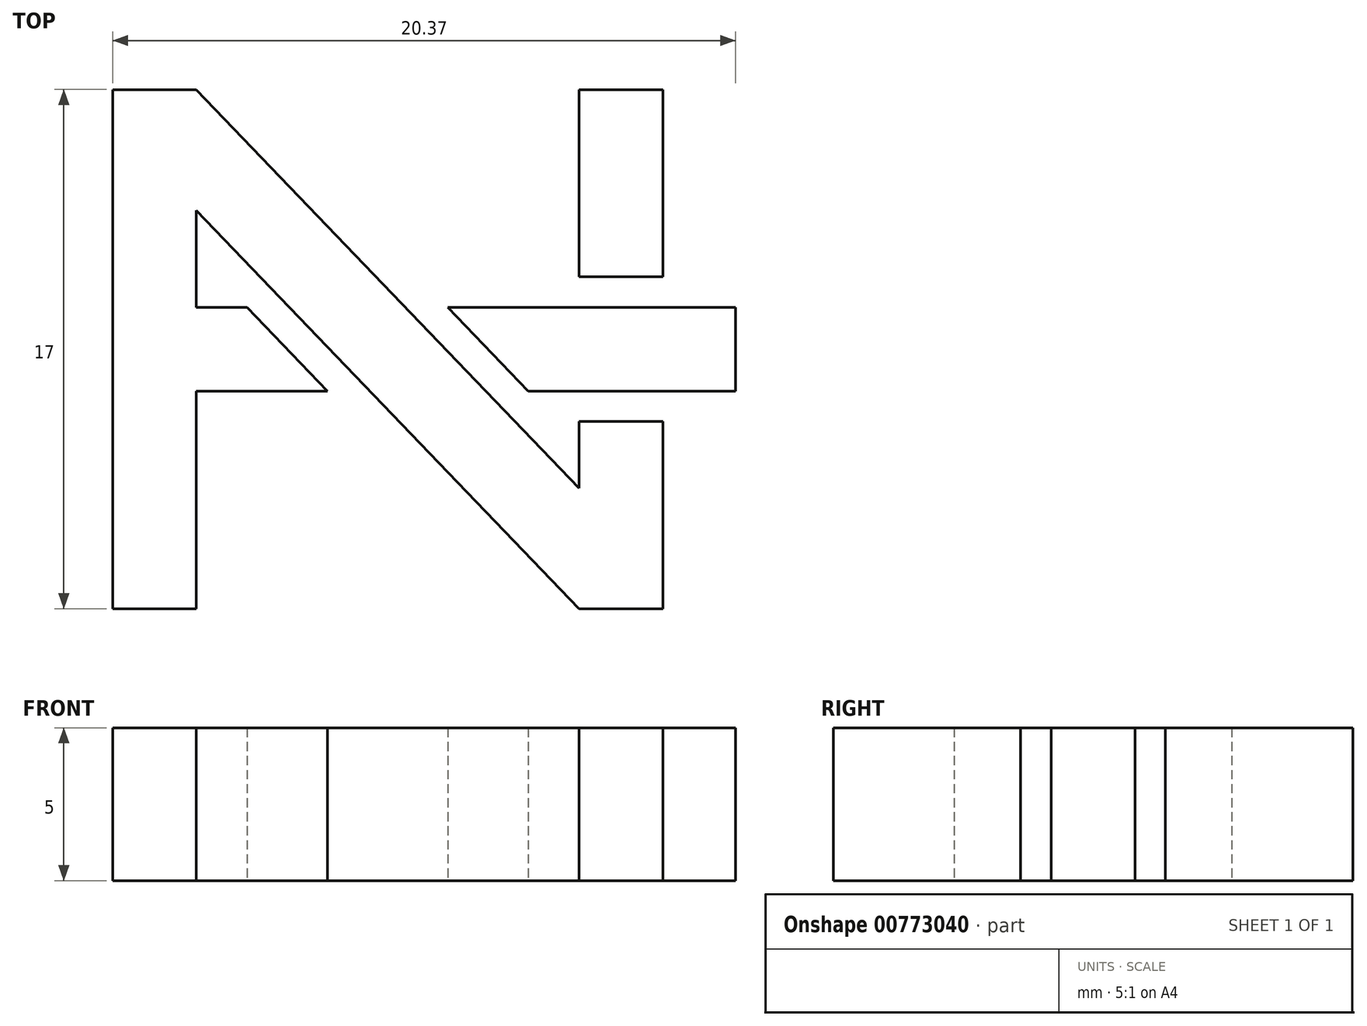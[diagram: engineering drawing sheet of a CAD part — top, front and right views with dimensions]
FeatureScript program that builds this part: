
annotation { "Feature Type Name" : "Feature", "Feature Type Description" : "" }
export const myFeature = defineFeature(function(context is Context, id is Id, definition is map)
    precondition{}
    {
        {
            var Q0;
            Q0=qCreatedBy(makeId("Top.planeOp"),FACE);
            var sketch = newSketch(context, id + "F0", { "sketchPlane" : qUnion([Q0])});
            skLineSegment(sketch, "E0", {"start": v(-16.47, -1.01) * mm, "end": v(11.53, -1.01) * mm, "construction": true});
            skLineSegment(sketch, "E1", {"start": v(-2.47, -15.01) * mm, "end": v(-2.47, 12.99) * mm, "construction": true});
            skLineSegment(sketch, "E2", {"start": v(-11.47, -9.51) * mm, "end": v(-11.47, 7.49) * mm});
            skLineSegment(sketch, "E3", {"start": v(6.53, -9.51) * mm, "end": v(6.53, -3.38) * mm});
            skLineSegment(sketch, "E4", {"start": v(-11.47, -9.51) * mm, "end": v(-8.73, -9.51) * mm});
            skLineSegment(sketch, "E5", {"start": v(-8.73, -9.51) * mm, "end": v(-8.73, -2.38) * mm});
            skLineSegment(sketch, "E6", {"start": v(-8.73, 7.49) * mm, "end": v(-11.47, 7.49) * mm});
            skLineSegment(sketch, "E7.MirrorCS", {"start": v(3.79, -5.56) * mm, "end": v(3.79, -3.38) * mm});
            skLineSegment(sketch, "E8.MirrorCS", {"start": v(6.53, -9.51) * mm, "end": v(3.79, -9.51) * mm});
            skLineSegment(sketch, "E9.MirrorCS", {"start": v(3.79, 7.49) * mm, "end": v(6.53, 7.49) * mm});
            skLineSegment(sketch, "E10", {"start": v(3.79, -5.56) * mm, "end": v(-8.73, 7.49) * mm});
            skLineSegment(sketch, "E11", {"start": v(3.79, -9.51) * mm, "end": v(-8.73, 3.53) * mm});
            skLineSegment(sketch, "E12", {"start": v(-8.73, 0.36) * mm, "end": v(-7.07, 0.36) * mm});
            skLineSegment(sketch, "E13", {"start": v(8.9, 0.36) * mm, "end": v(8.9, -2.38) * mm});
            skLineSegment(sketch, "E14", {"start": v(8.9, -2.38) * mm, "end": v(2.13, -2.38) * mm});
            skLineSegment(sketch, "E15", {"start": v(-4.44, -2.38) * mm, "end": v(-7.07, 0.36) * mm});
            skLineSegment(sketch, "E16", {"start": v(2.13, -2.38) * mm, "end": v(-0.5, 0.36) * mm});
            skLineSegment(sketch, "E17", {"start": v(3.79, -3.38) * mm, "end": v(6.53, -3.38) * mm});
            skLineSegment(sketch, "E18", {"start": v(3.79, 1.36) * mm, "end": v(6.53, 1.36) * mm});
            skLineSegment(sketch, "E19.trimOffspring", {"start": v(-4.44, -2.38) * mm, "end": v(-8.73, -2.38) * mm});
            skLineSegment(sketch, "E20.trimOffspring", {"start": v(-5.69, 0.36) * mm, "end": v(-1.9, 0.36) * mm});
            skLineSegment(sketch, "E21.trimOffspring", {"start": v(-0.5, 0.36) * mm, "end": v(8.9, 0.36) * mm});
            skLineSegment(sketch, "E22.trimOffspring", {"start": v(-8.73, 0.36) * mm, "end": v(-8.73, 3.53) * mm});
            skPoint(sketch, "E23.orphan", {"position": v(8.9, -3.38) * mm});
            skLineSegment(sketch, "E24.trimOffspring", {"start": v(6.53, 1.36) * mm, "end": v(6.53, 7.49) * mm});
            skLineSegment(sketch, "E25.trimOffspring", {"start": v(3.79, 1.36) * mm, "end": v(3.79, 7.49) * mm});
            skSolve(sketch);
        }
        {
            var Q0;
            Q0=makeQuery(id+"F0.imprint","IMPRINT",FACE,{"disambiguationData":[TD([[makeQuery(id+"F0.imprint","IMPRINT",EDGE,{"derivedFrom":sQuery(id+"F0.wireOp",EDGE,"E3")}),1.0]])]});
            var Q1;
            Q1=makeQuery(id+"F0.imprint","IMPRINT",FACE,{"disambiguationData":[TD([[makeQuery(id+"F0.imprint","IMPRINT",EDGE,{"derivedFrom":sQuery(id+"F0.wireOp",EDGE,"E2")}),-1.0]])]});
            var Q2;
            Q2=makeQuery(id+"F0.imprint","IMPRINT",FACE,{"disambiguationData":[TD([[makeQuery(id+"F0.imprint","IMPRINT",EDGE,{"derivedFrom":sQuery(id+"F0.wireOp",EDGE,"E9.MirrorCS")}),-1.0]])]});
            var Q3;
            Q3=makeQuery(id+"F0.imprint","IMPRINT",FACE,{"disambiguationData":[TD([[makeQuery(id+"F0.imprint","IMPRINT",EDGE,{"derivedFrom":sQuery(id+"F0.wireOp",EDGE,"E13")}),-1.0]])]});
            extrude(context, id + "F1", {"entities" : qUnion([Q0, Q1, Q2, Q3]), "depth" : 5 * mm, "offsetDistance" : 25 * mm});
        }
    });
